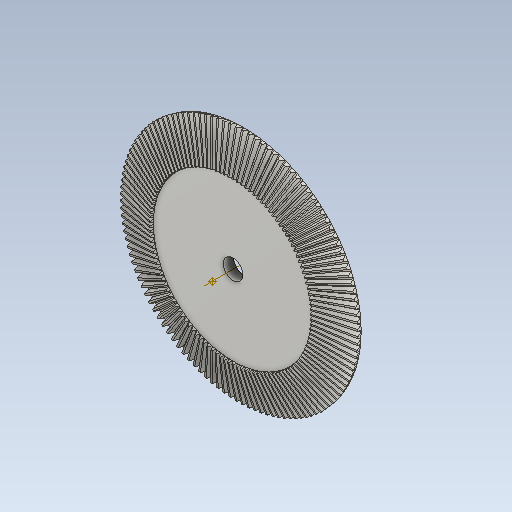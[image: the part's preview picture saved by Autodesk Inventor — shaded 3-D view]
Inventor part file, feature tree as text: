
AUTODESK INVENTOR PART (.ipt)
format: ipt  version: 2021 (Build 250183000, 183)  size: 1,540,608 bytes
history: native  units: mm
features: other x24, loft x2, pattern_circular x2, sketch x2, extrude x1
ambient origin geometry x6: Origin, XZ Plane, X Axis, Y Axis, Z Axis, Center Point
bodies: Solid1 (feature_tree)
feature tree (31):
  other  "Top Point"
  other  "Mesh Plane2"
  other  "Teeth Body"
  other  "Start Point"
  other  "Tooth Plane"
  other  "Start Sketch"
  other  "End Point"
  other  "3D Sketch Right"
  other  "End Plane Right"
  loft  "Loft Right"
  pattern_circular  "Circular Pattern Right"  [2 undecoded]
  other  "3D Sketch Left"
  other  "End Plane Left"
  loft  "Loft Left"
  pattern_circular  "Circular Pattern Left"  Angle=90.0deg  [1 undecoded]
  other  "Fix Body"
  extrude  "Extrusion1"  Depth=10.0mm
  other  "Mesh Plane"
  other  "Top Plane"
  other  "Teeth Body Sketch"
  other  "End Plane"
  other  "End Sketch"
  other  "Helical Curve Left"
  other  "End Sketch Left"
  other  "Body Sketch"
  sketch  "Sketch6"  dims[d0=152.4mm d1=151.660752mm]
  other  "Srf1"
  other  "Helical Curve Right"
  other  "End Sketch Right"
  sketch  "Sketch8"  dims[d2=153.01604mm d3=25.4mm d4=17.817919mm d5=90.0deg d7=107.900885mm d8=102.860474mm d9=278.590779mm d11=25.5397mm d12=72.815895mm d15=69.414421mm d16=188.004361mm d17=0.0mm d18=90.0deg d19=0.0mm d20=90.0deg d21=1200.0mm d22=360.0deg d26=267.453904mm d27=6.194287mm d28=152.4mm d29=-13.258177mm d30=72.815895mm d31=69.414421mm d32=188.004361mm d35=0.0mm d37=0.0mm d39=0.0mm d40=90.0deg d41=1200.0mm d42=360.0deg d46=90.0deg d47=90.0deg d48=0.0mm d49=0.0mm d50=90.0deg d51=0.261799mm d52=0.0mm d53=0.0mm d54=0.0mm d56=12.729302mm d57=316.288848mm d58=312.321368mm d59=213.444547mm d60=210.767131mm d61=213.444547mm d62=210.767131mm d63=90.0deg d64=90.0deg d65=267.453904mm d66=31.5mm d67=152.4mm d68=-13.258177mm d69=6.194287mm d70=69.414421mm d71=188.004361mm d72=72.815895mm d73=210.767131mm d74=213.444547mm d75=0.0mm d76=90.0deg d77=0.0mm d78=90.0deg d79=0.0mm d80=90.0deg d81=1200.0mm d82=360.0deg d84=10.0mm d85=20.0mm d86=20.0mm d87=10.0mm d88=0.0mm d89=0.0mm d90=12.7mm d91=0.0mm d92=0.0mm]
  other  "Pitch Diameter"
note: 3 required parameter values undecoded (feature->parameter linkage not recoverable at this tier; creation-order binding heuristic only, values carry confidence <= 0.55)
